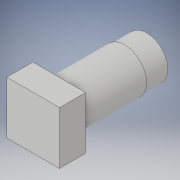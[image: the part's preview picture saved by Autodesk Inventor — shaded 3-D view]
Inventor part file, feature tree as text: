
AUTODESK INVENTOR PART (.ipt)
format: ipt  version: 2018 (Build 220112000, 112)  size: 109,056 bytes
history: native  units: in
note: dims shown in document units (in); Inventor stores cm internally (conversion verified against a paired STEP export)
features: extrude x3, sketch x3
ambient origin geometry x8: Origin, YZ Plane, XZ Plane, XY Plane, X Axis, Y Axis, Z Axis, Center Point
bodies: Solid1 (feature_tree)
feature tree (6):
  extrude  "Extrusion1"  Depth=0.6988in
  extrude  "Extrusion2"  Depth=0.3465in
  extrude  "Extrusion3"  Depth=0.2953in
  sketch  "Sketch1"  dims[d0=0.6988in d1=0.6988in]
  sketch  "Sketch2"  dims[d2=0.3465in d3=0.0in d4=0.5807in]
  sketch  "Sketch3"  dims[d5=0.8661in d6=0.0in d7=0.5556in d8=0.2953in d9=0.0in]
